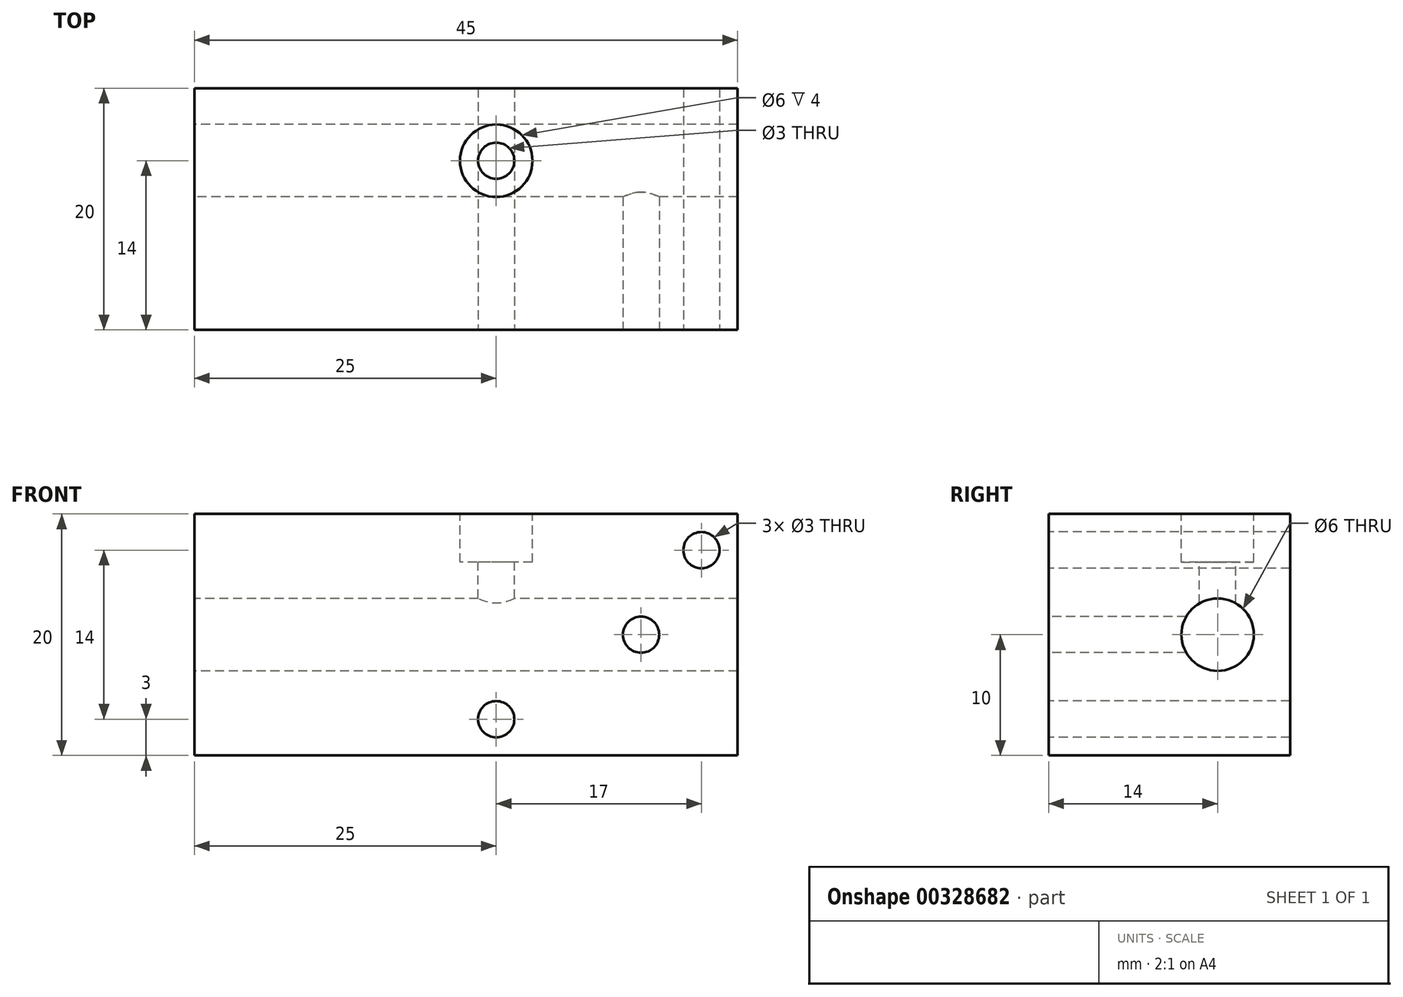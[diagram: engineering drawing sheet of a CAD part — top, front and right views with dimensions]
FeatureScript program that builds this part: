
annotation { "Feature Type Name" : "Feature", "Feature Type Description" : "" }
export const myFeature = defineFeature(function(context is Context, id is Id, definition is map)
    precondition{}
    {
        {
            var Q0;
            Q0=qCreatedBy(makeId("Front.planeOp"),FACE);
            var sketch = newSketch(context, id + "F0", { "sketchPlane" : qUnion([Q0])});
            skLineSegment(sketch, "E0.bottom", {"start": v(22.5, 10) * mm, "end": v(-22.5, 10) * mm});
            skLineSegment(sketch, "E0.top", {"start": v(22.5, -10) * mm, "end": v(-22.5, -10) * mm});
            skLineSegment(sketch, "E0.left", {"start": v(22.5, 10) * mm, "end": v(22.5, -10) * mm});
            skLineSegment(sketch, "E0.right", {"start": v(-22.5, 10) * mm, "end": v(-22.5, -10) * mm});
            skPoint(sketch, "E0.middle", {"position": v(0, 0) * mm});
            skSolve(sketch);
        }
        {
            var Q0;
            Q0 = qSketchRegion(id + "F0", true);
            extrude(context, id + "F1", {"entities" : qUnion([Q0]), "depth" : 10 * mm, "hasSecondDirection" : true, "secondDirectionOppositeDirection" : true, "secondDirectionDepth" : 10 * mm});
        }
        {
            var Q0;
            Q0=makeQuery(id+"F1.opExtrude","SWEPT_FACE",FACE,{"disambiguationData":[OSD([sQuery(id+"F0.wireOp",EDGE,"E0.right")])]});
            var sketch = newSketch(context, id + "F2", { "sketchPlane" : qUnion([Q0])});
            skCircle(sketch, "E1", {"center": v(-4, 0) * mm, "radius": 3 * mm});
            skSolve(sketch);
        }
        {
            var Q0;
            Q0 = qSketchRegion(id + "F2", true);
            extrude(context, id + "F3", {"entities" : qUnion([Q0]), "operationType" : NewBodyOperationType.REMOVE, "endBound" : BoundingType.THROUGH_ALL, "oppositeDirection" : true, "depth" : 25 * mm});
        }
        {
            var Q0;
            Q0=makeQuery(id+"F1.opExtrude","CAP_FACE",FACE,{"disambiguationData":[OSD([sQuery(id+"F0.wireOp",EDGE,"E0.bottom"),sQuery(id+"F0.wireOp",EDGE,"E0.top"),sQuery(id+"F0.wireOp",EDGE,"E0.left"),sQuery(id+"F0.wireOp",EDGE,"E0.right")])],"isStart":false});
            var sketch = newSketch(context, id + "F4", { "sketchPlane" : qUnion([Q0])});
            skCircle(sketch, "E2", {"center": v(19.5, 7) * mm, "radius": 1.5 * mm});
            skCircle(sketch, "E3", {"center": v(2.5, -7) * mm, "radius": 1.5 * mm});
            skSolve(sketch);
        }
        {
            var Q0;
            Q0 = qSketchRegion(id + "F4", true);
            extrude(context, id + "F5", {"entities" : qUnion([Q0]), "operationType" : NewBodyOperationType.REMOVE, "endBound" : BoundingType.THROUGH_ALL, "oppositeDirection" : true, "depth" : 25 * mm});
        }
        {
            var Q0;
            Q0=makeQuery(id+"F1.opExtrude","CAP_FACE",FACE,{"disambiguationData":[OSD([sQuery(id+"F0.wireOp",EDGE,"E0.bottom"),sQuery(id+"F0.wireOp",EDGE,"E0.top"),sQuery(id+"F0.wireOp",EDGE,"E0.left"),sQuery(id+"F0.wireOp",EDGE,"E0.right")])],"isStart":false});
            var sketch = newSketch(context, id + "F6", { "sketchPlane" : qUnion([Q0])});
            skCircle(sketch, "E4", {"center": v(14.5, 0) * mm, "radius": 1.5 * mm});
            skSolve(sketch);
        }
        {
            var Q0;
            Q0 = qSketchRegion(id + "F6", true);
            extrude(context, id + "F7", {"entities" : qUnion([Q0]), "operationType" : NewBodyOperationType.REMOVE, "endBound" : BoundingType.UP_TO_NEXT, "oppositeDirection" : true, "depth" : 25 * mm});
        }
        {
            var Q0;
            Q0=makeQuery(id+"F1.opExtrude","SWEPT_FACE",FACE,{"disambiguationData":[OSD([sQuery(id+"F0.wireOp",EDGE,"E0.bottom")])]});
            var sketch = newSketch(context, id + "F8", { "sketchPlane" : qUnion([Q0])});
            skCircle(sketch, "E5", {"center": v(2.5, 4) * mm, "radius": 3 * mm});
            skSolve(sketch);
        }
        {
            var Q0;
            Q0 = qSketchRegion(id + "F8", true);
            extrude(context, id + "F9", {"entities" : qUnion([Q0]), "operationType" : NewBodyOperationType.REMOVE, "oppositeDirection" : true, "depth" : 4 * mm});
        }
        {
            var Q0;
            Q0=makeQuery(id+"F9.boolean.opBoolean","COPY",FACE,{"derivedFrom":makeQuery(id+"F9.opExtrude","CAP_FACE",FACE,{"disambiguationData":[OSD([sQuery(id+"F8.wireOp",EDGE,"E5")])],"isStart":false})});
            var sketch = newSketch(context, id + "F10", { "sketchPlane" : qUnion([Q0])});
            skCircle(sketch, "E6", {"center": v(2.5, 4) * mm, "radius": 1.5 * mm});
            skSolve(sketch);
        }
        {
            var Q0;
            Q0 = qSketchRegion(id + "F10", true);
            extrude(context, id + "F11", {"entities" : qUnion([Q0]), "operationType" : NewBodyOperationType.REMOVE, "endBound" : BoundingType.UP_TO_NEXT, "oppositeDirection" : true, "depth" : 25 * mm});
        }
    });
